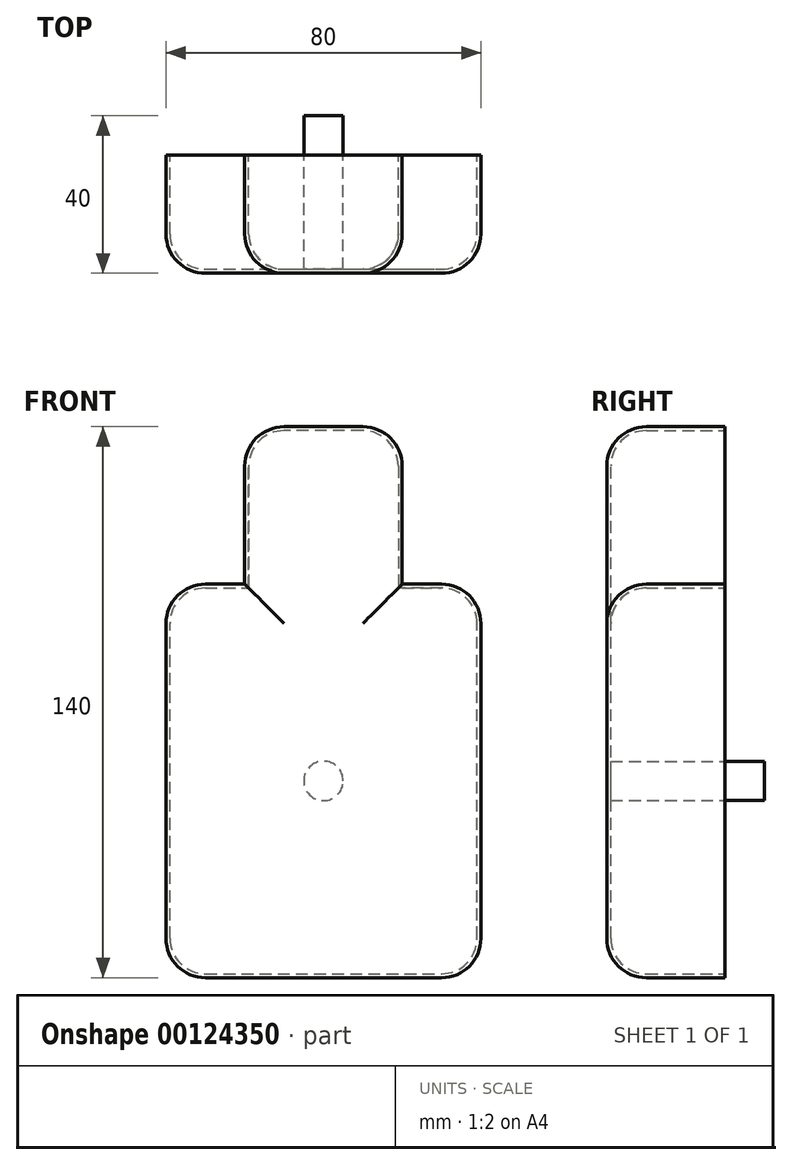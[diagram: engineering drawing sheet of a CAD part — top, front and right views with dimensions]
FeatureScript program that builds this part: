
annotation { "Feature Type Name" : "Feature", "Feature Type Description" : "" }
export const myFeature = defineFeature(function(context is Context, id is Id, definition is map)
    precondition{}
    {
        {
            var Q0;
            Q0=qCreatedBy(makeId("Front.planeOp"),FACE);
            var sketch = newSketch(context, id + "F0", { "sketchPlane" : qUnion([Q0])});
            skLineSegment(sketch, "E0.bottom", {"start": v(40, 50) * mm, "end": v(20, 50) * mm});
            skLineSegment(sketch, "E0.top", {"start": v(40, -50) * mm, "end": v(-40, -50) * mm});
            skLineSegment(sketch, "E0.left", {"start": v(40, 50) * mm, "end": v(40, -50) * mm});
            skLineSegment(sketch, "E0.right", {"start": v(-40, 50) * mm, "end": v(-40, -50) * mm});
            skPoint(sketch, "E0.middle", {"position": v(0, 0) * mm});
            skLineSegment(sketch, "E1.top", {"start": v(-20, 90) * mm, "end": v(20, 90) * mm});
            skLineSegment(sketch, "E1.left", {"start": v(-20, 50) * mm, "end": v(-20, 90) * mm});
            skLineSegment(sketch, "E1.right", {"start": v(20, 50) * mm, "end": v(20, 90) * mm});
            skLineSegment(sketch, "E2.trimOffspring", {"start": v(-20, 50) * mm, "end": v(-40, 50) * mm});
            skSolve(sketch);
        }
        {
            var Q0;
            Q0=makeQuery(id+"F0.imprint","IMPRINT",FACE,{"disambiguationData":[TD([[makeQuery(id+"F0.imprint","IMPRINT",EDGE,{"derivedFrom":sQuery(id+"F0.wireOp",EDGE,"E0.bottom")}),1.0]])]});
            extrude(context, id + "F1", {"entities" : qUnion([Q0]), "depth" : 40 * mm});
        }
        {
            var Q0;
            Q0=makeQuery(id+"F1.opExtrude","CAP_EDGE",EDGE,{"disambiguationData":[OSD([sQuery(id+"F0.wireOp",EDGE,"E0.left")])],"isStart":false});
            var Q1;
            Q1=makeQuery(id+"F1.opExtrude","CAP_EDGE",EDGE,{"disambiguationData":[OSD([sQuery(id+"F0.wireOp",EDGE,"E0.left")])],"isStart":true});
            var Q2;
            Q2=makeQuery(id+"F1.opExtrude","SWEPT_EDGE",EDGE,{"disambiguationData":[OSD([sQuery(id+"F0.wireOp",EDGE,"E0.bottom"),sQuery(id+"F0.wireOp",EDGE,"E0.left")])]});
            var Q3;
            Q3=makeQuery(id+"F1.opExtrude","CAP_EDGE",EDGE,{"disambiguationData":[OSD([sQuery(id+"F0.wireOp",EDGE,"E0.right")])],"isStart":false});
            var Q4;
            Q4=makeQuery(id+"F1.opExtrude","CAP_EDGE",EDGE,{"disambiguationData":[OSD([sQuery(id+"F0.wireOp",EDGE,"E0.right")])],"isStart":true});
            var Q5;
            Q5=makeQuery(id+"F1.opExtrude","CAP_EDGE",EDGE,{"disambiguationData":[OSD([sQuery(id+"F0.wireOp",EDGE,"E1.left")])],"isStart":false});
            var Q6;
            Q6=makeQuery(id+"F1.opExtrude","CAP_EDGE",EDGE,{"disambiguationData":[OSD([sQuery(id+"F0.wireOp",EDGE,"E1.left")])],"isStart":true});
            var Q7;
            Q7=makeQuery(id+"F1.opExtrude","CAP_EDGE",EDGE,{"disambiguationData":[OSD([sQuery(id+"F0.wireOp",EDGE,"E1.right")])],"isStart":false});
            var Q8;
            Q8=makeQuery(id+"F1.opExtrude","CAP_EDGE",EDGE,{"disambiguationData":[OSD([sQuery(id+"F0.wireOp",EDGE,"E1.right")])],"isStart":true});
            var Q9;
            Q9=makeQuery(id+"F1.opExtrude","CAP_EDGE",EDGE,{"disambiguationData":[OSD([sQuery(id+"F0.wireOp",EDGE,"E1.top")])],"isStart":false});
            var Q10;
            Q10=makeQuery(id+"F1.opExtrude","SWEPT_EDGE",EDGE,{"disambiguationData":[OSD([sQuery(id+"F0.wireOp",EDGE,"E1.top"),sQuery(id+"F0.wireOp",EDGE,"E1.left")])]});
            var Q11;
            Q11=makeQuery(id+"F1.opExtrude","SWEPT_EDGE",EDGE,{"disambiguationData":[OSD([sQuery(id+"F0.wireOp",EDGE,"E1.top"),sQuery(id+"F0.wireOp",EDGE,"E1.right")])]});
            var Q12;
            Q12=makeQuery(id+"F1.opExtrude","CAP_EDGE",EDGE,{"disambiguationData":[OSD([sQuery(id+"F0.wireOp",EDGE,"E1.top")])],"isStart":true});
            var Q13;
            Q13=makeQuery(id+"F1.opExtrude","CAP_EDGE",EDGE,{"disambiguationData":[OSD([sQuery(id+"F0.wireOp",EDGE,"E0.bottom")])],"isStart":false});
            var Q14;
            Q14=makeQuery(id+"F1.opExtrude","CAP_FACE",FACE,{"disambiguationData":[OSD([sQuery(id+"F0.wireOp",EDGE,"E0.bottom"),sQuery(id+"F0.wireOp",EDGE,"E0.top"),sQuery(id+"F0.wireOp",EDGE,"E0.left"),sQuery(id+"F0.wireOp",EDGE,"E0.right"),sQuery(id+"F0.wireOp",EDGE,"E1.top"),sQuery(id+"F0.wireOp",EDGE,"E1.left"),sQuery(id+"F0.wireOp",EDGE,"E1.right"),sQuery(id+"F0.wireOp",EDGE,"E2.trimOffspring")])],"isStart":false});
            var Q15;
            Q15=makeQuery(id+"F1.opExtrude","CAP_EDGE",EDGE,{"disambiguationData":[OSD([sQuery(id+"F0.wireOp",EDGE,"E2.trimOffspring")])],"isStart":true});
            var Q16;
            Q16=makeQuery(id+"F1.opExtrude","CAP_EDGE",EDGE,{"disambiguationData":[OSD([sQuery(id+"F0.wireOp",EDGE,"E0.bottom")])],"isStart":true});
            var Q17;
            Q17=makeQuery(id+"F1.opExtrude","CAP_EDGE",EDGE,{"disambiguationData":[OSD([sQuery(id+"F0.wireOp",EDGE,"E0.top")])],"isStart":true});
            var Q18;
            Q18=makeQuery(id+"F1.opExtrude","SWEPT_EDGE",EDGE,{"disambiguationData":[OSD([sQuery(id+"F0.wireOp",EDGE,"E0.top"),sQuery(id+"F0.wireOp",EDGE,"E0.left")])]});
            var Q19;
            Q19=makeQuery(id+"F1.opExtrude","SWEPT_EDGE",EDGE,{"disambiguationData":[OSD([sQuery(id+"F0.wireOp",EDGE,"E0.top"),sQuery(id+"F0.wireOp",EDGE,"E0.right")])]});
            var Q20;
            Q20=makeQuery(id+"F1.opExtrude","SWEPT_EDGE",EDGE,{"disambiguationData":[OSD([sQuery(id+"F0.wireOp",EDGE,"E0.right"),sQuery(id+"F0.wireOp",EDGE,"E2.trimOffspring")])]});
            fillet(context, id + "F2", {"entities" : qUnion([Q0, Q1, Q2, Q3, Q4, Q5, Q6, Q7, Q8, Q9, Q10, Q11, Q12, Q13, Q14, Q15, Q16, Q17, Q18, Q19, Q20]), "radius" : 10 * mm, "tangentPropagation" : true, "allowEdgeOverflow" : false});
        }
        {
            var Q0;
            Q0=makeQuery(id+"F1.opExtrude","CAP_FACE",FACE,{"disambiguationData":[OSD([sQuery(id+"F0.wireOp",EDGE,"E0.bottom"),sQuery(id+"F0.wireOp",EDGE,"E0.top"),sQuery(id+"F0.wireOp",EDGE,"E0.left"),sQuery(id+"F0.wireOp",EDGE,"E0.right"),sQuery(id+"F0.wireOp",EDGE,"E1.top"),sQuery(id+"F0.wireOp",EDGE,"E1.left"),sQuery(id+"F0.wireOp",EDGE,"E1.right"),sQuery(id+"F0.wireOp",EDGE,"E2.trimOffspring")])],"isStart":true});
            var Q1;
            {var subQ0=sQuery(id+"F0.wireOp",EDGE,"E1.top");Q1=makeQuery(id+"F2.opFillet","BLEND_FACE",FACE,{"disambiguationData":[OSD([subQ0]),TDD([makeQuery(id+"F1.opExtrude","CAP_EDGE",EDGE,{"disambiguationData":[OSD([subQ0])],"isStart":true})])]});}
            var Q2;
            {var subQ0=sQuery(id+"F0.wireOp",EDGE,"E1.left");Q2=makeQuery(id+"F2.opFillet","BLEND_FACE",FACE,{"disambiguationData":[OSD([subQ0]),TDD([makeQuery(id+"F1.opExtrude","CAP_EDGE",EDGE,{"disambiguationData":[OSD([subQ0])],"isStart":true})])]});}
            var Q3;
            {var subQ0=sQuery(id+"F0.wireOp",EDGE,"E1.left");var subQ1=sQuery(id+"F0.wireOp",EDGE,"E1.top");Q3=makeQuery(id+"F2.opFillet","BLEND_FACE",FACE,{"disambiguationData":[OSD([subQ1,subQ0]),TDD([makeQuery(id+"F1.opExtrude","CAP_VERTEX",VERTEX,{"disambiguationData":[OSD([subQ1,subQ0])],"isStart":true})])]});}
            var Q4;
            {var subQ0=sQuery(id+"F0.wireOp",EDGE,"E2.trimOffspring");Q4=makeQuery(id+"F2.opFillet","BLEND_FACE",FACE,{"disambiguationData":[OSD([subQ0]),TDD([makeQuery(id+"F1.opExtrude","CAP_EDGE",EDGE,{"disambiguationData":[OSD([subQ0])],"isStart":true})])]});}
            var Q5;
            {var subQ0=sQuery(id+"F0.wireOp",EDGE,"E2.trimOffspring");var subQ1=sQuery(id+"F0.wireOp",EDGE,"E0.right");Q5=makeQuery(id+"F2.opFillet","BLEND_FACE",FACE,{"disambiguationData":[OSD([subQ1,subQ0]),TDD([makeQuery(id+"F1.opExtrude","CAP_VERTEX",VERTEX,{"disambiguationData":[OSD([subQ1,subQ0])],"isStart":true})])]});}
            var Q6;
            {var subQ0=sQuery(id+"F0.wireOp",EDGE,"E0.right");Q6=makeQuery(id+"F2.opFillet","BLEND_FACE",FACE,{"disambiguationData":[OSD([subQ0]),TDD([makeQuery(id+"F1.opExtrude","CAP_EDGE",EDGE,{"disambiguationData":[OSD([subQ0])],"isStart":true})])]});}
            var Q7;
            {var subQ0=sQuery(id+"F0.wireOp",EDGE,"E0.right");var subQ1=sQuery(id+"F0.wireOp",EDGE,"E0.top");Q7=makeQuery(id+"F2.opFillet","BLEND_FACE",FACE,{"disambiguationData":[OSD([subQ1,subQ0]),TDD([makeQuery(id+"F1.opExtrude","CAP_VERTEX",VERTEX,{"disambiguationData":[OSD([subQ1,subQ0])],"isStart":true})])]});}
            var Q8;
            {var subQ0=sQuery(id+"F0.wireOp",EDGE,"E0.top");Q8=makeQuery(id+"F2.opFillet","BLEND_FACE",FACE,{"disambiguationData":[OSD([subQ0]),TDD([makeQuery(id+"F1.opExtrude","CAP_EDGE",EDGE,{"disambiguationData":[OSD([subQ0])],"isStart":true})])]});}
            var Q9;
            {var subQ0=sQuery(id+"F0.wireOp",EDGE,"E0.left");var subQ1=sQuery(id+"F0.wireOp",EDGE,"E0.top");Q9=makeQuery(id+"F2.opFillet","BLEND_FACE",FACE,{"disambiguationData":[OSD([subQ1,subQ0]),TDD([makeQuery(id+"F1.opExtrude","CAP_VERTEX",VERTEX,{"disambiguationData":[OSD([subQ1,subQ0])],"isStart":true})])]});}
            var Q10;
            {var subQ0=sQuery(id+"F0.wireOp",EDGE,"E0.left");Q10=makeQuery(id+"F2.opFillet","BLEND_FACE",FACE,{"disambiguationData":[OSD([subQ0]),TDD([makeQuery(id+"F1.opExtrude","CAP_EDGE",EDGE,{"disambiguationData":[OSD([subQ0])],"isStart":true})])]});}
            var Q11;
            {var subQ0=sQuery(id+"F0.wireOp",EDGE,"E0.left");var subQ1=sQuery(id+"F0.wireOp",EDGE,"E0.bottom");Q11=makeQuery(id+"F2.opFillet","BLEND_FACE",FACE,{"disambiguationData":[OSD([subQ1,subQ0]),TDD([makeQuery(id+"F1.opExtrude","CAP_VERTEX",VERTEX,{"disambiguationData":[OSD([subQ1,subQ0])],"isStart":true})])]});}
            var Q12;
            {var subQ0=sQuery(id+"F0.wireOp",EDGE,"E0.bottom");Q12=makeQuery(id+"F2.opFillet","BLEND_FACE",FACE,{"disambiguationData":[OSD([subQ0]),TDD([makeQuery(id+"F1.opExtrude","CAP_EDGE",EDGE,{"disambiguationData":[OSD([subQ0])],"isStart":true})])]});}
            var Q13;
            {var subQ0=sQuery(id+"F0.wireOp",EDGE,"E1.right");Q13=makeQuery(id+"F2.opFillet","BLEND_FACE",FACE,{"disambiguationData":[OSD([subQ0]),TDD([makeQuery(id+"F1.opExtrude","CAP_EDGE",EDGE,{"disambiguationData":[OSD([subQ0])],"isStart":true})])]});}
            var Q14;
            {var subQ0=sQuery(id+"F0.wireOp",EDGE,"E1.right");var subQ1=sQuery(id+"F0.wireOp",EDGE,"E1.top");Q14=makeQuery(id+"F2.opFillet","BLEND_FACE",FACE,{"disambiguationData":[OSD([subQ1,subQ0]),TDD([makeQuery(id+"F1.opExtrude","CAP_VERTEX",VERTEX,{"disambiguationData":[OSD([subQ1,subQ0])],"isStart":true})])]});}
            shell(context, id + "F3", {"entities" : qUnion([Q0, Q1, Q2, Q3, Q4, Q5, Q6, Q7, Q8, Q9, Q10, Q11, Q12, Q13, Q14]), "thickness" : 1 * mm});
        }
        {
            var Q0;
            Q0=qCreatedBy(makeId("Front.planeOp"),FACE);
            var sketch = newSketch(context, id + "F4", { "sketchPlane" : qUnion([Q0])});
            skCircle(sketch, "E3", {"center": v(0, 0) * mm, "radius": 5 * mm});
            skSolve(sketch);
        }
        {
            var Q0;
            Q0=makeQuery(id+"F4.imprint","IMPRINT",FACE,{"disambiguationData":[TD([[makeQuery(id+"F4.imprint","IMPRINT",EDGE,{"derivedFrom":sQuery(id+"F4.wireOp",EDGE,"E3")}),1.0]])]});
            var Q1;
            Q1=makeQuery(id+"F3.opShell","OFFSET_FACE",FACE,{"disambiguationData":[OSD([sQuery(id+"F0.wireOp",EDGE,"E0.bottom"),sQuery(id+"F0.wireOp",EDGE,"E0.top"),sQuery(id+"F0.wireOp",EDGE,"E0.left"),sQuery(id+"F0.wireOp",EDGE,"E0.right"),sQuery(id+"F0.wireOp",EDGE,"E1.top"),sQuery(id+"F0.wireOp",EDGE,"E1.left"),sQuery(id+"F0.wireOp",EDGE,"E1.right"),sQuery(id+"F0.wireOp",EDGE,"E2.trimOffspring")])]});
            extrude(context, id + "F5", {"entities" : qUnion([Q0]), "operationType" : NewBodyOperationType.ADD, "endBound" : BoundingType.UP_TO_SURFACE, "endBoundEntityFace" : qUnion([Q1]), "depth" : 25 * mm});
        }
    });
